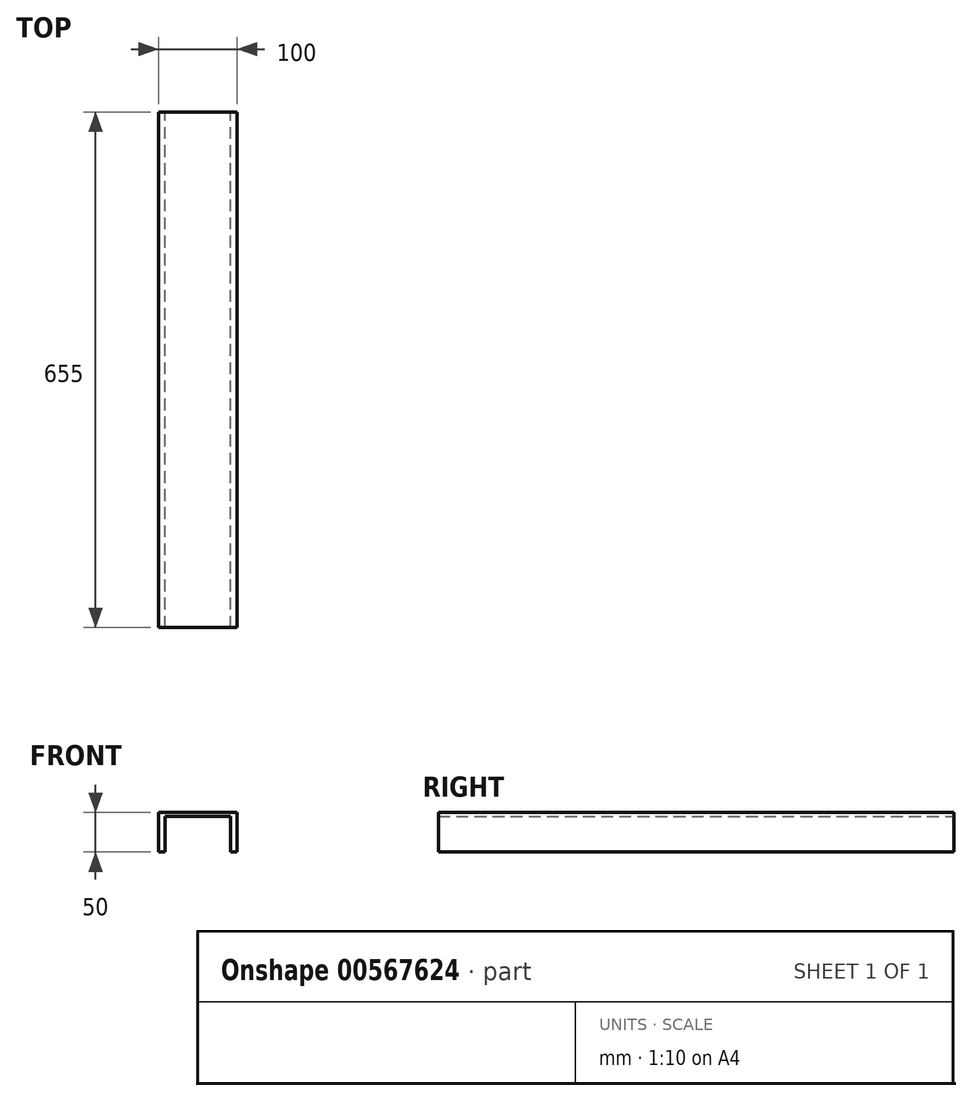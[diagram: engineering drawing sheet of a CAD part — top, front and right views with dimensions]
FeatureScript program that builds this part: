
annotation { "Feature Type Name" : "Feature", "Feature Type Description" : "" }
export const myFeature = defineFeature(function(context is Context, id is Id, definition is map)
    precondition{}
    {
        {
            var Q0;
            Q0=qCreatedBy(makeId("Front.planeOp"),FACE);
            var sketch = newSketch(context, id + "F0", { "sketchPlane" : qUnion([Q0])});
            skLineSegment(sketch, "E0", {"start": v(-47.76, 39.74) * mm, "end": v(52.24, 39.74) * mm});
            skLineSegment(sketch, "E1", {"start": v(-47.76, 39.74) * mm, "end": v(-47.76, -10.26) * mm});
            skLineSegment(sketch, "E2", {"start": v(52.24, 39.74) * mm, "end": v(52.24, -10.26) * mm});
            skLineSegment(sketch, "E3", {"start": v(52.24, -10.26) * mm, "end": v(43.74, -10.26) * mm});
            skLineSegment(sketch, "E4", {"start": v(43.74, -10.26) * mm, "end": v(43.74, 34.74) * mm});
            skLineSegment(sketch, "E5", {"start": v(43.74, 34.74) * mm, "end": v(-39.26, 34.74) * mm});
            skLineSegment(sketch, "E6", {"start": v(-39.26, 34.74) * mm, "end": v(-39.26, -10.26) * mm});
            skLineSegment(sketch, "E7", {"start": v(-39.26, -10.26) * mm, "end": v(-47.76, -10.26) * mm});
            skSolve(sketch);
        }
        {
            var Q0;
            Q0=qSketchRegion(id+"F0",true);
            extrude(context, id + "F1", {"entities" : qUnion([Q0]), "depth" : 655 * mm, "offsetDistance" : 25 * mm});
        }
    });
